# Revit family: 1427xxx Astro Avignon Wall Round 525 (CE)_ RFA
name_source: partatom
category: Lighting Fixtures
units: mm (PartAtom-declared; Revit-internal decimal feet)

## family parameters
Always vertical = Yes
Cut with Voids When Loaded = No
Host = Wall
Light Source = No
OmniClass Number = 23.80.70.00
OmniClass Title = Lighting
Part Type = Normal
Room Calculation Point = No
Round Connector Dimension = Use Diameter
Shared = No

## types (2) — shared parameters
ADA compliant = N / A
Dimmable = yes
Dimming Method = lamp Dependent
Driver Included = no
Driver Required = No
Efficacy (lm/w) = Lamp Dependent
Electrical Class ( CE ) = 1
Lamp = 2 X E27
Location / IP Rating = Indoor / IP20
Main Material = Metal - Steel / Zinc
Manufacturer = Astro Lighting Ltd
Manufacturer URL - Europe and Rest of World = www.astrolighting.com
Manufacturer URL - North America = us.astrolighting.com
Power (Watts) = 12 W Max
Product Dimensions (MM) = 525 X 126 x 99
Product Location = Wall Light
Product Name = Avignon Round 525
Product URL = https://www.astrolighting.com
Product Weight (KG) = 3.6
URL = www.astrolighting.com
zero-valued in all types: Default Elevation

## per-type parameters (varying)
| type | Main Finish | Product SKU |
| Avignon Wall Round 525 Bronze | Bronze / Glass | 1427003 |
| Avignon Wall Round 525 Antique Brass | Antique Brass  / Glass | 1427004 |

## geometry (parser evidence)
native form markers: Sweep x2
no freeform markers — native parametric forms only
